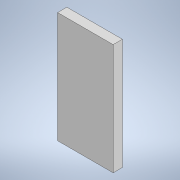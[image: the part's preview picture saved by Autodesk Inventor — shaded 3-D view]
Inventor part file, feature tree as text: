
AUTODESK INVENTOR PART (.ipt)
format: ipt  version: 2022 (Build 260153000, 153)  size: 91,648 bytes
history: native  units: mm
features: other x1, extrude x1, sketch x1
ambient origin geometry x8: Origin, YZ Plane, XZ Plane, XY Plane, X Axis, Y Axis, Z Axis, Center Point
bodies: Body1 (feature_tree)
feature tree (3):
  other  "ソリッド1"
  extrude  "押し出し1"  Depth=5.0mm
  sketch  "スケッチ1"
